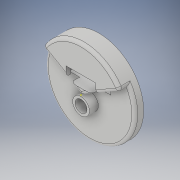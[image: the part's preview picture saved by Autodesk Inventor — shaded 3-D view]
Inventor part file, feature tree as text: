
AUTODESK INVENTOR PART (.ipt)
format: ipt  version: 2019 (Build 230136000, 136)  size: 203,776 bytes
history: native  units: in
note: dims shown in document units (in); Inventor stores cm internally (conversion verified against a paired STEP export)
features: sketch x7, extrude x5, fillet x2, hole x1
ambient origin geometry x8: Origin, YZ Plane, XZ Plane, XY Plane, X Axis, Y Axis, Z Axis, Center Point
bodies: Solid1 (feature_tree)
feature tree (15):
  extrude  "Extrusion1"  Depth=0.5906in TaperAngle=0.0deg
  extrude  "Extrusion2"  TaperAngle=30.0deg  [1 undecoded]
  hole  "Hole1"  [1 undecoded]
  extrude  "Extrusion3"  Depth=0.7874in
  fillet  "Fillet1"  Radius=1.1024in
  fillet  "Fillet2"  Radius=0.5906in
  sketch  "Sketch5"  dims[d21=0.7874in d22=0.2362in d23=0.1575in d24=0.0787in d25=90.0deg d26=1.1811in d27=0.8108in d28=1.1024in d29=0.5906in d30=0.0in]
  extrude  "Extrusion4"  Depth=0.1969in
  extrude  "Extrusion5"  Depth=2.3622in
  sketch  "Sketch1"  dims[d5=0.5906in d6=0.0in d12=0.5906in d13=0.0in]
  sketch  "Sketch2"  dims[d14=2.9528in d15=30.0deg]
  sketch  "Sketch3"  dims[d16=2.9528in d17=1.0306in]
  sketch  "Sketch4"  dims[d18=2.9528in d20=0.7874in]
  sketch  "Sketch6"  dims[d31=0.1969in d32=0.1969in]
  sketch  "Sketch7"  dims[d46=0.8661in d47=0.0in d61=2.3622in d62=0.7874in d63=0.9843in d64=0.7874in d65=0.9843in d66=0.9843in d68=0.9843in d69=0.5906in d70=0.0in d71=0.3937in d72=1.378in d73=1.7717in d74=2.7559in d75=1.7717in]
note: 2 required parameter values undecoded (feature->parameter linkage not recoverable at this tier; creation-order binding heuristic only, values carry confidence <= 0.55)
